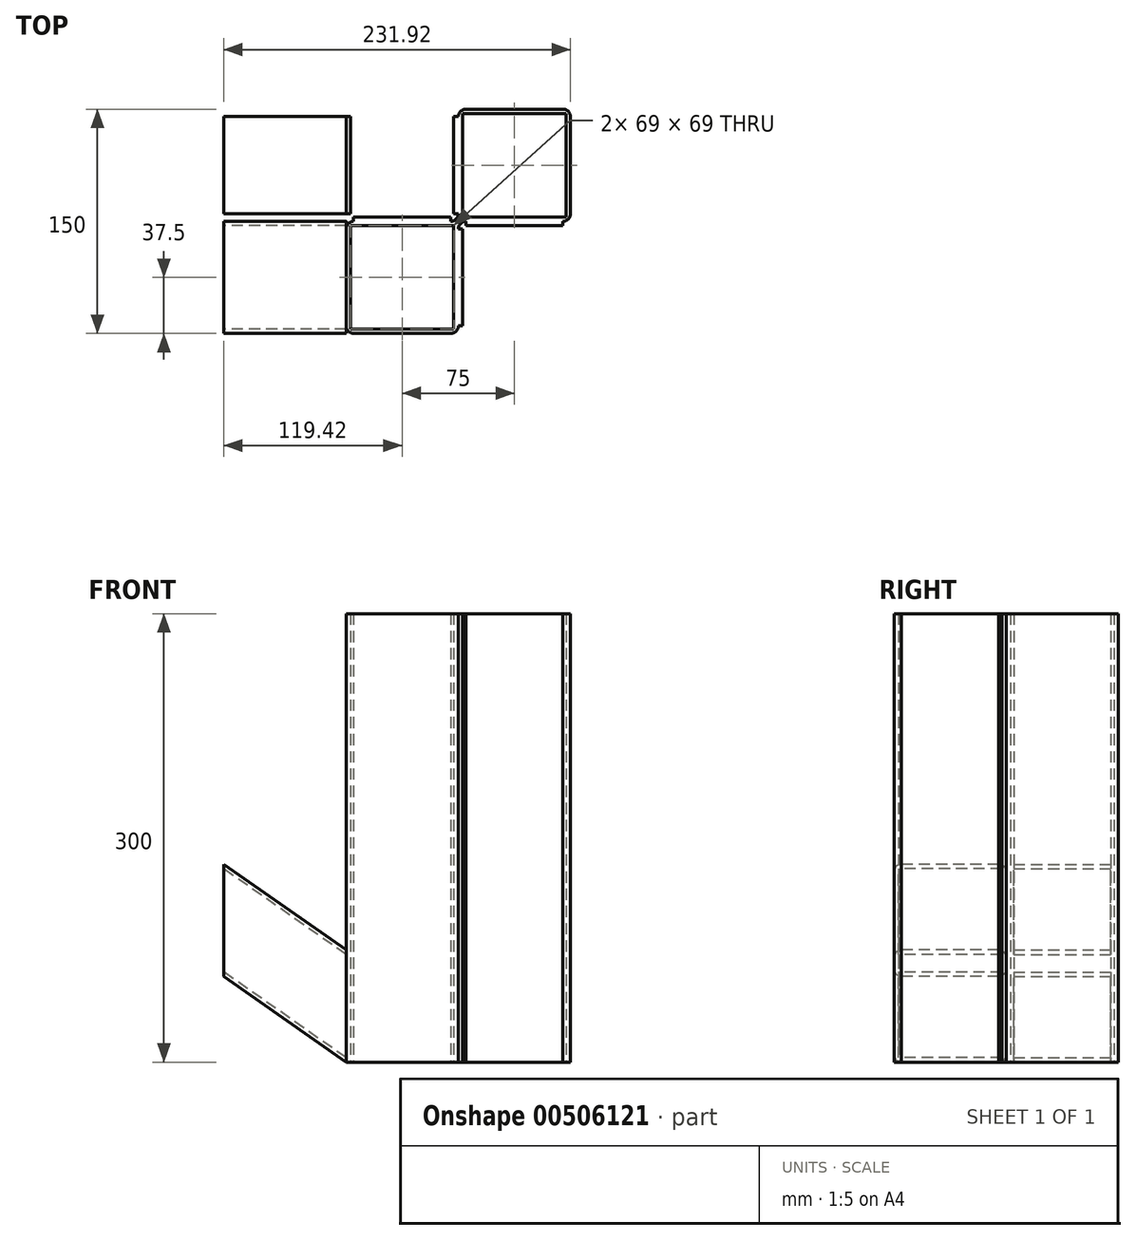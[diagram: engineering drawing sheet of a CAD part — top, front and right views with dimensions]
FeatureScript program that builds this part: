
annotation { "Feature Type Name" : "Feature", "Feature Type Description" : "" }
export const myFeature = defineFeature(function(context is Context, id is Id, definition is map)
    precondition{}
    {
        {
            var Q0;
            Q0=qCreatedBy(makeId("Top.planeOp"),FACE);
            var sketch = newSketch(context, id + "F0", { "sketchPlane" : qUnion([Q0])});
            skLineSegment(sketch, "E0.bottom", {"start": v(5, 0) * mm, "end": v(70, 0) * mm});
            skLineSegment(sketch, "E0.top", {"start": v(5, 75) * mm, "end": v(70, 75) * mm});
            skLineSegment(sketch, "E0.left", {"start": v(0, 5) * mm, "end": v(0, 70) * mm});
            skLineSegment(sketch, "E0.right", {"start": v(75, 5) * mm, "end": v(75, 70) * mm});
            skPoint(sketch, "E1.visualSharp", {"position": v(0, 75) * mm});
            skArc(sketch, "E1.filletArc", {"start": v(5, 75) * mm, "mid": v(1.46, 73.54) * mm, "end": v(0, 70) * mm});
            skPoint(sketch, "E2.visualSharp", {"position": v(75, 75) * mm});
            skArc(sketch, "E2.filletArc", {"start": v(75, 70) * mm, "mid": v(73.54, 73.54) * mm, "end": v(70, 75) * mm});
            skPoint(sketch, "E3.visualSharp", {"position": v(75, 0) * mm});
            skArc(sketch, "E3.filletArc", {"start": v(70, 0) * mm, "mid": v(73.54, 1.46) * mm, "end": v(75, 5) * mm});
            skPoint(sketch, "E4.visualSharp", {"position": v(0, 0) * mm});
            skArc(sketch, "E4.filletArc", {"start": v(0, 5) * mm, "mid": v(1.46, 1.46) * mm, "end": v(5, 0) * mm});
            skLineSegment(sketch, "E5.0", {"start": v(3, 72) * mm, "end": v(72, 72) * mm});
            skLineSegment(sketch, "E5.1", {"start": v(3, 3) * mm, "end": v(3, 72) * mm});
            skLineSegment(sketch, "E5.2", {"start": v(3, 3) * mm, "end": v(72, 3) * mm});
            skLineSegment(sketch, "E5.3", {"start": v(72, 3) * mm, "end": v(72, 72) * mm});
            skArc(sketch, "E6.MirrorCS", {"start": v(-75, 70) * mm, "mid": v(-73.54, 73.54) * mm, "end": v(-70, 75) * mm});
            skArc(sketch, "E7.MirrorCS", {"start": v(0, 5) * mm, "mid": v(-1.46, 1.46) * mm, "end": v(-5, 0) * mm});
            skArc(sketch, "E8.MirrorCS", {"start": v(-5, 75) * mm, "mid": v(-1.46, 73.54) * mm, "end": v(0, 70) * mm});
            skArc(sketch, "E9.MirrorCS", {"start": v(-70, 0) * mm, "mid": v(-73.54, 1.46) * mm, "end": v(-75, 5) * mm});
            skLineSegment(sketch, "E10.MirrorCS", {"start": v(-5, 75) * mm, "end": v(-70, 75) * mm});
            skLineSegment(sketch, "E11.MirrorCS", {"start": v(-3, 72) * mm, "end": v(-72, 72) * mm});
            skLineSegment(sketch, "E12.MirrorCS", {"start": v(-3, 3) * mm, "end": v(-3, 72) * mm});
            skLineSegment(sketch, "E13.MirrorCS", {"start": v(-3, 3) * mm, "end": v(-72, 3) * mm});
            skLineSegment(sketch, "E14.MirrorCS", {"start": v(-72, 3) * mm, "end": v(-72, 72) * mm});
            skLineSegment(sketch, "E15.MirrorCS", {"start": v(-5, 0) * mm, "end": v(-70, 0) * mm});
            skLineSegment(sketch, "E16.MirrorCS", {"start": v(-75, 5) * mm, "end": v(-75, 70) * mm});
            skPoint(sketch, "E17.MirrorP", {"position": v(-75, 75) * mm});
            skPoint(sketch, "E18.MirrorP", {"position": v(-75, 0) * mm});
            skArc(sketch, "E19.MirrorCS", {"start": v(70, 0) * mm, "mid": v(73.54, -1.46) * mm, "end": v(75, -5) * mm});
            skArc(sketch, "E20.MirrorCS", {"start": v(5, -75) * mm, "mid": v(1.46, -73.54) * mm, "end": v(0, -70) * mm});
            skArc(sketch, "E21.MirrorCS", {"start": v(0, -5) * mm, "mid": v(-1.46, -1.46) * mm, "end": v(-5, 0) * mm});
            skArc(sketch, "E22.MirrorCS", {"start": v(-75, -70) * mm, "mid": v(-73.54, -73.54) * mm, "end": v(-70, -75) * mm});
            skArc(sketch, "E23.MirrorCS", {"start": v(75, -70) * mm, "mid": v(73.54, -73.54) * mm, "end": v(70, -75) * mm});
            skArc(sketch, "E24.MirrorCS", {"start": v(-5, -75) * mm, "mid": v(-1.46, -73.54) * mm, "end": v(0, -70) * mm});
            skArc(sketch, "E25.MirrorCS", {"start": v(0, -5) * mm, "mid": v(1.46, -1.46) * mm, "end": v(5, 0) * mm});
            skArc(sketch, "E26.MirrorCS", {"start": v(-70, 0) * mm, "mid": v(-73.54, -1.46) * mm, "end": v(-75, -5) * mm});
            skPoint(sketch, "E27.MirrorP", {"position": v(0, -75) * mm});
            skPoint(sketch, "E28.MirrorP", {"position": v(-75, -75) * mm});
            skLineSegment(sketch, "E29.MirrorCS", {"start": v(0, -5) * mm, "end": v(0, -70) * mm});
            skLineSegment(sketch, "E30.MirrorCS", {"start": v(-72, -3) * mm, "end": v(-72, -72) * mm});
            skLineSegment(sketch, "E31.MirrorCS", {"start": v(3, -3) * mm, "end": v(3, -72) * mm});
            skPoint(sketch, "E32.MirrorP", {"position": v(75, -75) * mm});
            skLineSegment(sketch, "E33.MirrorCS", {"start": v(75, -5) * mm, "end": v(75, -70) * mm});
            skLineSegment(sketch, "E34.MirrorCS", {"start": v(-5, -75) * mm, "end": v(-70, -75) * mm});
            skLineSegment(sketch, "E35.MirrorCS", {"start": v(3, -72) * mm, "end": v(72, -72) * mm});
            skLineSegment(sketch, "E36.MirrorCS", {"start": v(-3, -3) * mm, "end": v(-3, -72) * mm});
            skLineSegment(sketch, "E37.MirrorCS", {"start": v(5, -75) * mm, "end": v(70, -75) * mm});
            skLineSegment(sketch, "E38.MirrorCS", {"start": v(-3, -3) * mm, "end": v(-72, -3) * mm});
            skLineSegment(sketch, "E39.MirrorCS", {"start": v(-75, -5) * mm, "end": v(-75, -70) * mm});
            skLineSegment(sketch, "E40.MirrorCS", {"start": v(72, -3) * mm, "end": v(72, -72) * mm});
            skLineSegment(sketch, "E41.MirrorCS", {"start": v(3, -3) * mm, "end": v(72, -3) * mm});
            skLineSegment(sketch, "E42.MirrorCS", {"start": v(-3, -72) * mm, "end": v(-72, -72) * mm});
            skLineSegment(sketch, "E43", {"start": v(0, 70) * mm, "end": v(-3, 70) * mm});
            skLineSegment(sketch, "E44", {"start": v(0, 70) * mm, "end": v(3, 70) * mm});
            skLineSegment(sketch, "E45", {"start": v(0, 5) * mm, "end": v(-3, 5) * mm});
            skLineSegment(sketch, "E46", {"start": v(0, 5) * mm, "end": v(3, 5) * mm});
            skLineSegment(sketch, "E47", {"start": v(-5, 0) * mm, "end": v(-5, 3) * mm});
            skLineSegment(sketch, "E48", {"start": v(-5, 0) * mm, "end": v(-5, -3) * mm});
            skLineSegment(sketch, "E49", {"start": v(-70, 0) * mm, "end": v(-70, -3) * mm});
            skLineSegment(sketch, "E50", {"start": v(-70, 0) * mm, "end": v(-70, 3) * mm});
            skLineSegment(sketch, "E51", {"start": v(5, 0) * mm, "end": v(5, 3) * mm});
            skLineSegment(sketch, "E52", {"start": v(5, 0) * mm, "end": v(5, -3) * mm});
            skLineSegment(sketch, "E53", {"start": v(0, -5) * mm, "end": v(3, -5) * mm});
            skLineSegment(sketch, "E54", {"start": v(0, -5) * mm, "end": v(-3, -5) * mm});
            skLineSegment(sketch, "E55", {"start": v(70, 0) * mm, "end": v(70, -3) * mm});
            skLineSegment(sketch, "E56", {"start": v(70, 0) * mm, "end": v(70, 3) * mm});
            skLineSegment(sketch, "E57", {"start": v(0, -70) * mm, "end": v(3, -70) * mm});
            skLineSegment(sketch, "E58", {"start": v(0, -70) * mm, "end": v(-3, -70) * mm});
            skLineSegment(sketch, "E59", {"start": v(-75, 70) * mm, "end": v(-72, 70) * mm});
            skLineSegment(sketch, "E60", {"start": v(-75, 5) * mm, "end": v(-72, 5) * mm});
            skLineSegment(sketch, "E61", {"start": v(-75, -5) * mm, "end": v(-72, -5) * mm});
            skLineSegment(sketch, "E62", {"start": v(-75, -70) * mm, "end": v(-72, -70) * mm});
            skSolve(sketch);
        }
        {
            var Q0;
            Q0=makeQuery(id+"F0.imprint","IMPRINT",FACE,{"disambiguationData":[TD([[makeQuery(id+"F0.imprint","IMPRINT",EDGE,{"derivedFrom":sQuery(id+"F0.wireOp",EDGE,"E15.MirrorCS")}),1.0]])]});
            var Q1;
            Q1=makeQuery(id+"F0.imprint","IMPRINT",FACE,{"disambiguationData":[TD([[makeQuery(id+"F0.imprint","IMPRINT",EDGE,{"derivedFrom":sQuery(id+"F0.wireOp",EDGE,"E0.left")}),1.0]])]});
            var Q2;
            Q2=makeQuery(id+"F0.imprint","IMPRINT",FACE,{"disambiguationData":[TD([[makeQuery(id+"F0.imprint","IMPRINT",EDGE,{"derivedFrom":sQuery(id+"F0.wireOp",EDGE,"E0.bottom")}),1.0]])]});
            var Q3;
            Q3=makeQuery(id+"F0.imprint","IMPRINT",FACE,{"disambiguationData":[TD([[makeQuery(id+"F0.imprint","IMPRINT",EDGE,{"derivedFrom":sQuery(id+"F0.wireOp",EDGE,"E0.bottom")}),-1.0]])]});
            var Q4;
            Q4=makeQuery(id+"F0.imprint","IMPRINT",FACE,{"disambiguationData":[TD([[makeQuery(id+"F0.imprint","IMPRINT",EDGE,{"derivedFrom":sQuery(id+"F0.wireOp",EDGE,"E0.top")}),-1.0]])]});
            var Q5;
            Q5=makeQuery(id+"F0.imprint","IMPRINT",FACE,{"disambiguationData":[TD([[makeQuery(id+"F0.imprint","IMPRINT",EDGE,{"derivedFrom":sQuery(id+"F0.wireOp",EDGE,"E4.filletArc")}),1.0]])]});
            var Q6;
            Q6=makeQuery(id+"F0.imprint","IMPRINT",FACE,{"disambiguationData":[TD([[makeQuery(id+"F0.imprint","IMPRINT",EDGE,{"derivedFrom":sQuery(id+"F0.wireOp",EDGE,"E0.left")}),-1.0]])]});
            var Q7;
            Q7=makeQuery(id+"F0.imprint","IMPRINT",FACE,{"disambiguationData":[TD([[makeQuery(id+"F0.imprint","IMPRINT",EDGE,{"derivedFrom":sQuery(id+"F0.wireOp",EDGE,"E7.MirrorCS")}),-1.0]])]});
            var Q8;
            Q8=makeQuery(id+"F0.imprint","IMPRINT",FACE,{"disambiguationData":[TD([[makeQuery(id+"F0.imprint","IMPRINT",EDGE,{"derivedFrom":sQuery(id+"F0.wireOp",EDGE,"E15.MirrorCS")}),-1.0]])]});
            var Q9;
            Q9=makeQuery(id+"F0.imprint","IMPRINT",FACE,{"disambiguationData":[TD([[makeQuery(id+"F0.imprint","IMPRINT",EDGE,{"derivedFrom":sQuery(id+"F0.wireOp",EDGE,"E6.MirrorCS")}),-1.0]])]});
            var Q10;
            Q10=makeQuery(id+"F0.imprint","IMPRINT",FACE,{"disambiguationData":[TD([[makeQuery(id+"F0.imprint","IMPRINT",EDGE,{"derivedFrom":sQuery(id+"F0.wireOp",EDGE,"E22.MirrorCS")}),1.0]])]});
            var Q11;
            Q11=makeQuery(id+"F0.imprint","IMPRINT",FACE,{"disambiguationData":[TD([[makeQuery(id+"F0.imprint","IMPRINT",EDGE,{"derivedFrom":sQuery(id+"F0.wireOp",EDGE,"E29.MirrorCS")}),-1.0]])]});
            var Q12;
            Q12=makeQuery(id+"F0.imprint","IMPRINT",FACE,{"disambiguationData":[TD([[makeQuery(id+"F0.imprint","IMPRINT",EDGE,{"derivedFrom":sQuery(id+"F0.wireOp",EDGE,"E21.MirrorCS")}),1.0]])]});
            var Q13;
            Q13=makeQuery(id+"F0.imprint","IMPRINT",FACE,{"disambiguationData":[TD([[makeQuery(id+"F0.imprint","IMPRINT",EDGE,{"derivedFrom":sQuery(id+"F0.wireOp",EDGE,"E25.MirrorCS")}),-1.0]])]});
            var Q14;
            Q14=makeQuery(id+"F0.imprint","IMPRINT",FACE,{"disambiguationData":[TD([[makeQuery(id+"F0.imprint","IMPRINT",EDGE,{"derivedFrom":sQuery(id+"F0.wireOp",EDGE,"E29.MirrorCS")}),1.0]])]});
            var Q15;
            Q15=makeQuery(id+"F0.imprint","IMPRINT",FACE,{"disambiguationData":[TD([[makeQuery(id+"F0.imprint","IMPRINT",EDGE,{"derivedFrom":sQuery(id+"F0.wireOp",EDGE,"E19.MirrorCS")}),-1.0]])]});
            var Q16;
            Q16=makeQuery(id+"F0.imprint","IMPRINT",FACE,{"disambiguationData":[TD([[makeQuery(id+"F0.imprint","IMPRINT",EDGE,{"derivedFrom":sQuery(id+"F0.wireOp",EDGE,"E16.MirrorCS")}),-1.0]])]});
            var Q17;
            Q17=makeQuery(id+"F0.imprint","IMPRINT",FACE,{"disambiguationData":[TD([[makeQuery(id+"F0.imprint","IMPRINT",EDGE,{"derivedFrom":sQuery(id+"F0.wireOp",EDGE,"E9.MirrorCS")}),-1.0]])]});
            var Q18;
            Q18=makeQuery(id+"F0.imprint","IMPRINT",FACE,{"disambiguationData":[TD([[makeQuery(id+"F0.imprint","IMPRINT",EDGE,{"derivedFrom":sQuery(id+"F0.wireOp",EDGE,"E26.MirrorCS")}),1.0]])]});
            var Q19;
            Q19=makeQuery(id+"F0.imprint","IMPRINT",FACE,{"disambiguationData":[TD([[makeQuery(id+"F0.imprint","IMPRINT",EDGE,{"derivedFrom":sQuery(id+"F0.wireOp",EDGE,"E39.MirrorCS")}),1.0]])]});
            extrude(context, id + "F1", {"entities" : qUnion([Q0, Q1, Q2, Q3, Q4, Q5, Q6, Q7, Q8, Q9, Q10, Q11, Q12, Q13, Q14, Q15, Q16, Q17, Q18, Q19]), "depth" : 300 * mm});
        }
        {
            var Q0;
            Q0=qCreatedBy(makeId("Front.planeOp"),FACE);
            var sketch = newSketch(context, id + "F2", { "sketchPlane" : qUnion([Q0])});
            skLineSegment(sketch, "E63.0", {"start": v(-75, 300) * mm, "end": v(-75, 0) * mm});
            skLineSegment(sketch, "E64", {"start": v(-75, 0) * mm, "end": v(-156.92, 57.36) * mm});
            skLineSegment(sketch, "E65", {"start": v(-75, 0) * mm, "end": v(-86.7, 0) * mm});
            skSolve(sketch);
        }
        {
            var Q0;
            Q0=makeQuery(id+"F1.opExtrude","SWEPT_FACE",FACE,{"disambiguationData":[OSD([sQuery(id+"F0.wireOp",EDGE,"E16.MirrorCS")])]});
            var sketch = newSketch(context, id + "F3", { "sketchPlane" : qUnion([Q0])});
            skLineSegment(sketch, "E66", {"start": v(5, 0) * mm, "end": v(70, 0) * mm});
            skLineSegment(sketch, "E67.0", {"start": v(5, 75) * mm, "end": v(70, 75) * mm});
            skLineSegment(sketch, "E68", {"start": v(-75, 75) * mm, "end": v(-75, 0) * mm});
            skLineSegment(sketch, "E69", {"start": v(0, 70) * mm, "end": v(0, 5) * mm});
            skLineSegment(sketch, "E70", {"start": v(75, 70) * mm, "end": v(75, 5) * mm});
            skPoint(sketch, "E71.visualSharp", {"position": v(0, 75) * mm});
            skArc(sketch, "E71.filletArc", {"start": v(5, 75) * mm, "mid": v(1.46, 73.54) * mm, "end": v(0, 70) * mm});
            skPoint(sketch, "E72.visualSharp", {"position": v(75, 75) * mm});
            skArc(sketch, "E72.filletArc", {"start": v(75, 70) * mm, "mid": v(73.54, 73.54) * mm, "end": v(70, 75) * mm});
            skPoint(sketch, "E73.visualSharp", {"position": v(75, 0) * mm});
            skArc(sketch, "E73.filletArc", {"start": v(70, 0) * mm, "mid": v(73.54, 1.46) * mm, "end": v(75, 5) * mm});
            skPoint(sketch, "E74.visualSharp", {"position": v(0, 0) * mm});
            skArc(sketch, "E74.filletArc", {"start": v(0, 5) * mm, "mid": v(1.46, 1.46) * mm, "end": v(5, 0) * mm});
            skLineSegment(sketch, "E75.0", {"start": v(3, 72) * mm, "end": v(72, 72) * mm});
            skLineSegment(sketch, "E75.1", {"start": v(3, 72) * mm, "end": v(3, 3) * mm});
            skLineSegment(sketch, "E75.2", {"start": v(3, 3) * mm, "end": v(72, 3) * mm});
            skLineSegment(sketch, "E75.3", {"start": v(72, 72) * mm, "end": v(72, 3) * mm});
            skLineSegment(sketch, "E76.0", {"start": v(0, -5) * mm, "end": v(75, -5) * mm});
            skLineSegment(sketch, "E76.1", {"start": v(0, 305) * mm, "end": v(0, -5) * mm});
            skLineSegment(sketch, "E76.2", {"start": v(75, 305) * mm, "end": v(0, 305) * mm});
            skLineSegment(sketch, "E76.3", {"start": v(75, -5) * mm, "end": v(75, 305) * mm});
            skArc(sketch, "E77.MirrorCS", {"start": v(-75, 70) * mm, "mid": v(-73.54, 73.54) * mm, "end": v(-70, 75) * mm});
            skLineSegment(sketch, "E78.MirrorCS", {"start": v(-5, 75) * mm, "end": v(-70, 75) * mm});
            skArc(sketch, "E79.MirrorCS", {"start": v(-70, 0) * mm, "mid": v(-73.54, 1.46) * mm, "end": v(-75, 5) * mm});
            skArc(sketch, "E80.MirrorCS", {"start": v(-5, 75) * mm, "mid": v(-1.46, 73.54) * mm, "end": v(0, 70) * mm});
            skLineSegment(sketch, "E81.MirrorCS", {"start": v(-3, 3) * mm, "end": v(-72, 3) * mm});
            skPoint(sketch, "E82.MirrorP", {"position": v(-75, 75) * mm});
            skLineSegment(sketch, "E83.MirrorCS", {"start": v(-72, 72) * mm, "end": v(-72, 3) * mm});
            skLineSegment(sketch, "E84.MirrorCS", {"start": v(-3, 72) * mm, "end": v(-3, 3) * mm});
            skLineSegment(sketch, "E85.MirrorCS", {"start": v(-3, 72) * mm, "end": v(-72, 72) * mm});
            skArc(sketch, "E86.MirrorCS", {"start": v(0, 5) * mm, "mid": v(-1.46, 1.46) * mm, "end": v(-5, 0) * mm});
            skPoint(sketch, "E87.MirrorP", {"position": v(-75, 0) * mm});
            skLineSegment(sketch, "E88.MirrorCS", {"start": v(-75, 70) * mm, "end": v(-75, 5) * mm});
            skLineSegment(sketch, "E89.MirrorCS", {"start": v(-5, 0) * mm, "end": v(-70, 0) * mm});
            skSolve(sketch);
        }
        {
            var Q0;
            {var subQ5=sQuery(id+"F3.wireOp",EDGE,"E77.MirrorCS");Q0=makeQuery(id+"F3.imprint","IMPRINT",FACE,{"disambiguationData":[TD([[makeQuery(id+"F3.imprint","IMPRINT",EDGE,{"derivedFrom":subQ5}),-1.0]])]});}
            var Q1;
            {var subQ0=sQuery(id+"F3.wireOp",EDGE,"E78.MirrorCS");Q1=makeQuery(id+"F3.imprint","IMPRINT",FACE,{"disambiguationData":[TD([[makeQuery(id+"F3.imprint","IMPRINT",EDGE,{"derivedFrom":subQ0}),1.0]])]});}
            var Q2;
            {var subQ6=sQuery(id+"F3.wireOp",EDGE,"E80.MirrorCS");Q2=makeQuery(id+"F3.imprint","IMPRINT",FACE,{"disambiguationData":[TD([[makeQuery(id+"F3.imprint","IMPRINT",EDGE,{"derivedFrom":subQ6}),-1.0]])]});}
            var Q3;
            {var subQ6=sQuery(id+"F3.wireOp",EDGE,"E89.MirrorCS");Q3=makeQuery(id+"F3.imprint","IMPRINT",FACE,{"disambiguationData":[TD([[makeQuery(id+"F3.imprint","IMPRINT",EDGE,{"derivedFrom":subQ6}),-1.0]])]});}
            var Q4;
            Q4=makeQuery(id+"F3.imprint","IMPRINT",FACE,{"disambiguationData":[TD([[makeQuery(id+"F3.imprint","IMPRINT",EDGE,{"derivedFrom":sQuery(id+"F3.wireOp",EDGE,"E66")}),1.0]])]});
            var Q5;
            Q5=sQuery(id+"F2.wireOp",EDGE,"E64");
            sweep(context, id + "F4", {"profiles" : qUnion([Q0, Q1, Q2, Q3, Q4]), "path" : qUnion([Q5])});
        }
    });
